# Revit family: Roxtec RS seals
name_source: partatom
category: Duct Accessories
revit_build: Autodesk Revit 2017 (Build: 20190508_0315(x64)
units: mm (PartAtom-declared; Revit-internal decimal feet)

## family parameters
Cut with Voids When Loaded = No
Host = Face
Part Type = Attaches To
Round Connector Dimension = Use Diameter
Shared = No

## types (10) — shared parameters
Core material = Roxylon black
Description = Sealing solutions for cables and pipes
ETIM Classification = EC000220
Fitting material = Steel
Fitting thickness = 5 mm  [stored 0.0164042 ft]
Frame material = Roxylon blue
Manufacturer = Roxtec
Sealing material = Roxylon blue
URL = https://www.roxtec.com
Version = 2.0
zero-valued in all types: Default Elevation, NominalDepth, NominalHeight

## per-type parameters (varying)
| type | Front fitting diameter | Max cable Ø | Min cable Ø | Sealing height | Sähkönumero | Wall opening diameter | Weight (kg) | core visibility |
| RS 25 | 32 mm  [stored 0.104987 ft] | 12 mm  [stored 0.0393701 ft] | 4 mm  [stored 0.0131234 ft] | 32 mm  [stored 0.104987 ft] | 1753087 | 25 mm  [stored 0.082021 ft] | 0.04 | Yes |
| RS 50 | 60 mm | 30 mm  [stored 0.0984252 ft] | 8 mm  [stored 0.0262467 ft] | 75 mm  [stored 0.246063 ft] | 1753089 | 50 mm  [stored 0.164042 ft] | 0.32 | Yes |
| RS 75 | 85 mm  [stored 0.278871 ft] | 54 mm  [stored 0.177165 ft] | 24 mm  [stored 0.0787402 ft] | 75 mm  [stored 0.246063 ft] | 1753091 | 75 mm  [stored 0.246063 ft] | 0.6 | Yes |
| RS 100 WOC | 110 mm  [stored 0.360892 ft] | 70 mm  [stored 0.229659 ft] | 48 mm  [stored 0.15748 ft] | 75 mm  [stored 0.246063 ft] | 1753092 | 100 mm  [stored 0.328084 ft] | 0.8 | No |
| RS 125 WOC | 135 mm  [stored 0.442913 ft] | 98 mm  [stored 0.321522 ft] | 66 mm  [stored 0.216535 ft] | 75 mm  [stored 0.246063 ft] | 1753092 | 125 mm  [stored 0.410105 ft] | 1.2 | No |
| RS 150 WOC | 160 mm  [stored 0.524934 ft] | 119 mm  [stored 0.39042 ft] | 93 mm  [stored 0.305118 ft] | 75 mm  [stored 0.246063 ft] | 1753092 | 150 mm  [stored 0.492126 ft] | 1.6 | No |
| RS 175 WOC | 185 mm  [stored 0.606955 ft] | 145 mm  [stored 0.475722 ft] | 119 mm  [stored 0.39042 ft] | 75 mm  [stored 0.246063 ft] | 1753092 | 175 mm  [stored 0.574147 ft] | 2.3 | No |
| RS 200 WOC | 210 mm  [stored 0.688976 ft] | 170 mm  [stored 0.557743 ft] | 138 mm  [stored 0.452756 ft] | 75 mm  [stored 0.246063 ft] | 1753092 | 200 mm  [stored 0.656168 ft] | 2.7 | No |
| RS 250 WOC | 260 mm | 206 mm  [stored 0.675853 ft] | 176 mm  [stored 0.577428 ft] | 75 mm  [stored 0.246063 ft] | 1753092 | 250 mm  [stored 0.82021 ft] | 3.3 | No |
| RS 225 WOC | 235 mm  [stored 0.770997 ft] | 181 mm  [stored 0.593832 ft] | 151 mm  [stored 0.495407 ft] | 75 mm  [stored 0.246063 ft] | 1753092 | 225 mm  [stored 0.738189 ft] | 3.2 | No |

note: [stored X ft] marks values corroborated as IEEE doubles in the binary element streams (Revit-internal decimal feet)

## geometry (parser evidence)
native form markers: Sweep x3
no freeform markers — native parametric forms only
